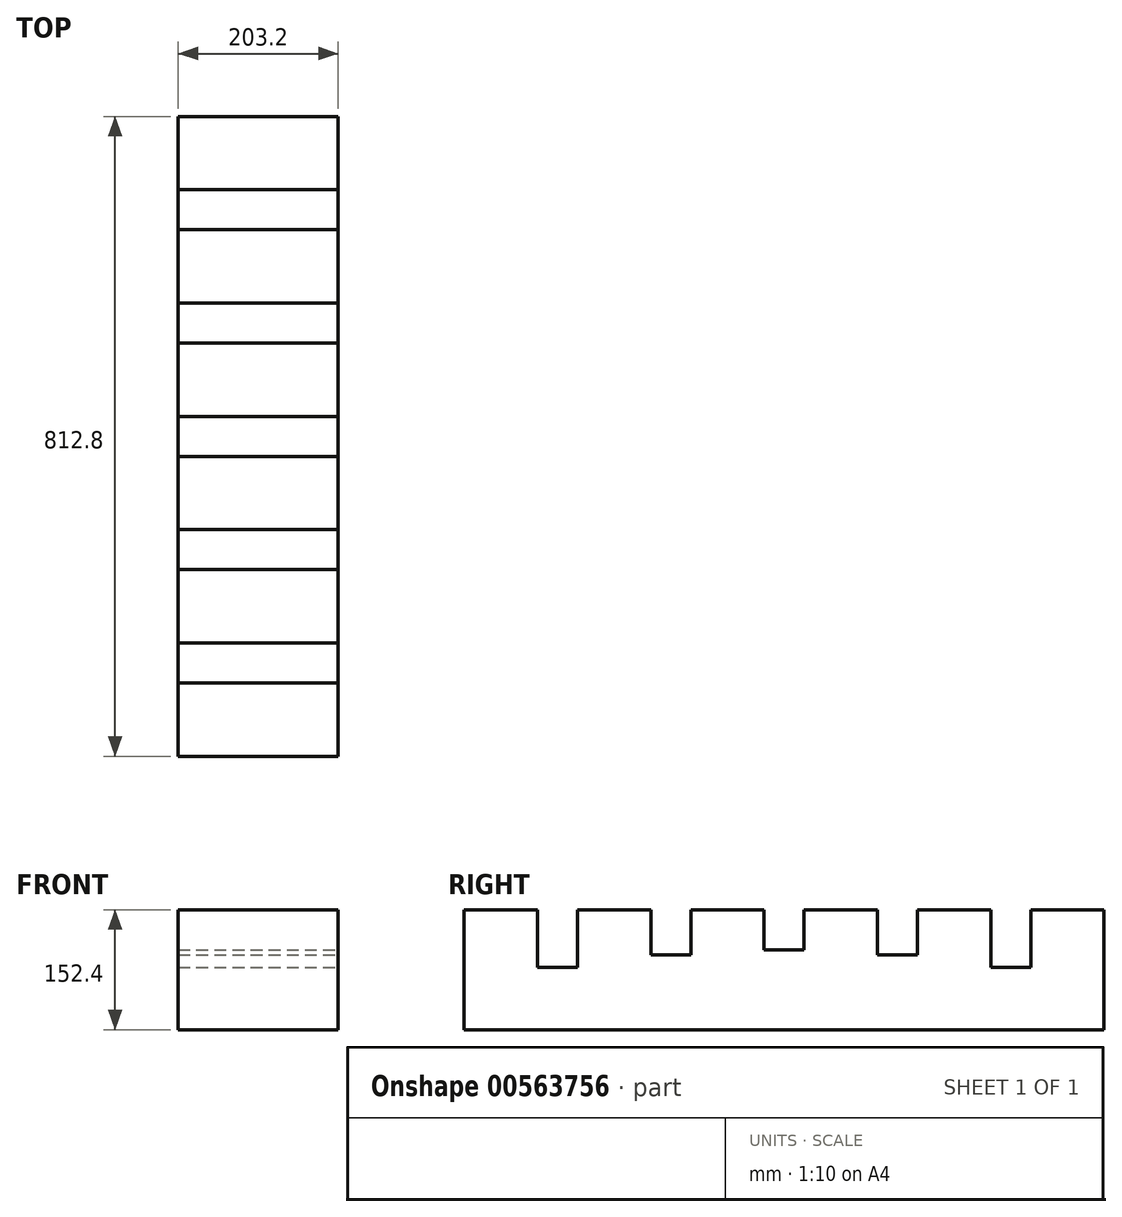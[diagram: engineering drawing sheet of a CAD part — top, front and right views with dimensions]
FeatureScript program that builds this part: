
annotation { "Feature Type Name" : "Feature", "Feature Type Description" : "" }
export const myFeature = defineFeature(function(context is Context, id is Id, definition is map)
    precondition{}
    {
        {
            var Q0;
            Q0=qCreatedBy(makeId("Front.planeOp"),FACE);
            var sketch = newSketch(context, id + "F0", { "sketchPlane" : qUnion([Q0])});
            skLineSegment(sketch, "E0.bottom", {"start": v(101.6, 76.2) * mm, "end": v(-101.6, 76.2) * mm});
            skLineSegment(sketch, "E0.top", {"start": v(101.6, -76.2) * mm, "end": v(-101.6, -76.2) * mm});
            skLineSegment(sketch, "E0.left", {"start": v(101.6, 76.2) * mm, "end": v(101.6, -76.2) * mm});
            skLineSegment(sketch, "E0.right", {"start": v(-101.6, 76.2) * mm, "end": v(-101.6, -76.2) * mm});
            skPoint(sketch, "E0.middle", {"position": v(0, 0) * mm});
            skSolve(sketch);
        }
        {
            var Q0;
            Q0=qSketchRegion(id+"F0",true);
            extrude(context, id + "F1", {"entities" : qUnion([Q0]), "endBound" : BoundingType.SYMMETRIC, "depth" : 812.8 * mm, "offsetDistance" : 25.4 * mm});
        }
        {
            var Q0;
            Q0=makeQuery(id+"F1.opExtrude","SWEPT_FACE",FACE,{"disambiguationData":[OSD([sQuery(id+"F0.wireOp",EDGE,"E0.left")])]});
            var sketch = newSketch(context, id + "F2", { "sketchPlane" : qUnion([Q0])});
            skLineSegment(sketch, "E1.bottom", {"start": v(25.4, 25.4) * mm, "end": v(-25.4, 25.4) * mm});
            skLineSegment(sketch, "E1.top", {"start": v(25.4, 114.3) * mm, "end": v(-25.4, 114.3) * mm});
            skLineSegment(sketch, "E1.left", {"start": v(25.4, 25.4) * mm, "end": v(25.4, 114.3) * mm});
            skLineSegment(sketch, "E1.right", {"start": v(-25.4, 25.4) * mm, "end": v(-25.4, 114.3) * mm});
            skPoint(sketch, "E1.middle", {"position": v(0, 69.85) * mm});
            skLineSegment(sketch, "E2.bottom", {"start": v(-118.53, 18.96) * mm, "end": v(-169.33, 18.96) * mm});
            skLineSegment(sketch, "E2.top", {"start": v(-118.53, 107.86) * mm, "end": v(-169.33, 107.86) * mm});
            skLineSegment(sketch, "E2.left", {"start": v(-118.53, 18.96) * mm, "end": v(-118.53, 107.86) * mm});
            skLineSegment(sketch, "E2.right", {"start": v(-169.33, 18.96) * mm, "end": v(-169.33, 107.86) * mm});
            skPoint(sketch, "E2.middle", {"position": v(-143.93, 63.4) * mm});
            skLineSegment(sketch, "E3.bottom", {"start": v(-262.47, 2.9) * mm, "end": v(-313.27, 2.9) * mm});
            skLineSegment(sketch, "E3.top", {"start": v(-262.47, 91.8) * mm, "end": v(-313.27, 91.8) * mm});
            skLineSegment(sketch, "E3.left", {"start": v(-262.47, 2.9) * mm, "end": v(-262.47, 91.8) * mm});
            skLineSegment(sketch, "E3.right", {"start": v(-313.27, 2.9) * mm, "end": v(-313.27, 91.8) * mm});
            skPoint(sketch, "E3.middle", {"position": v(-287.87, 47.35) * mm});
            skLineSegment(sketch, "E4.bottom", {"start": v(169.33, 18.96) * mm, "end": v(118.53, 18.96) * mm});
            skLineSegment(sketch, "E4.top", {"start": v(169.33, 107.86) * mm, "end": v(118.53, 107.86) * mm});
            skLineSegment(sketch, "E4.left", {"start": v(169.33, 18.96) * mm, "end": v(169.33, 107.86) * mm});
            skLineSegment(sketch, "E4.right", {"start": v(118.53, 18.96) * mm, "end": v(118.53, 107.86) * mm});
            skPoint(sketch, "E4.middle", {"position": v(143.93, 63.4) * mm});
            skLineSegment(sketch, "E5.bottom", {"start": v(313.27, 2.9) * mm, "end": v(262.47, 2.9) * mm});
            skLineSegment(sketch, "E5.top", {"start": v(313.27, 91.8) * mm, "end": v(262.47, 91.8) * mm});
            skLineSegment(sketch, "E5.left", {"start": v(313.27, 2.9) * mm, "end": v(313.27, 91.8) * mm});
            skLineSegment(sketch, "E5.right", {"start": v(262.47, 2.9) * mm, "end": v(262.47, 91.8) * mm});
            skPoint(sketch, "E5.middle", {"position": v(287.87, 47.35) * mm});
            skCircle(sketch, "E6", {"center": v(0, -2063.75) * mm, "radius": 2178.2 * mm, "construction": true});
            skLineSegment(sketch, "E7", {"start": v(-313.27, 47.35) * mm, "end": v(-406.4, 47.35) * mm, "construction": true});
            skLineSegment(sketch, "E8", {"start": v(-169.33, 63.4) * mm, "end": v(-262.47, 63.4) * mm, "construction": true});
            skLineSegment(sketch, "E9", {"start": v(-25.4, 69.85) * mm, "end": v(-118.53, 69.85) * mm, "construction": true});
            skPoint(sketch, "E9.endSnap0", {"position": v(-118.53, 63.4) * mm});
            skSolve(sketch);
        }
        {
            var Q0;
            Q0=qSketchRegion(id+"F2",true);
            extrude(context, id + "F3", {"entities" : qUnion([Q0]), "operationType" : NewBodyOperationType.REMOVE, "endBound" : BoundingType.THROUGH_ALL, "oppositeDirection" : true, "depth" : 198.12 * mm, "offsetDistance" : 25.4 * mm});
        }
    });
